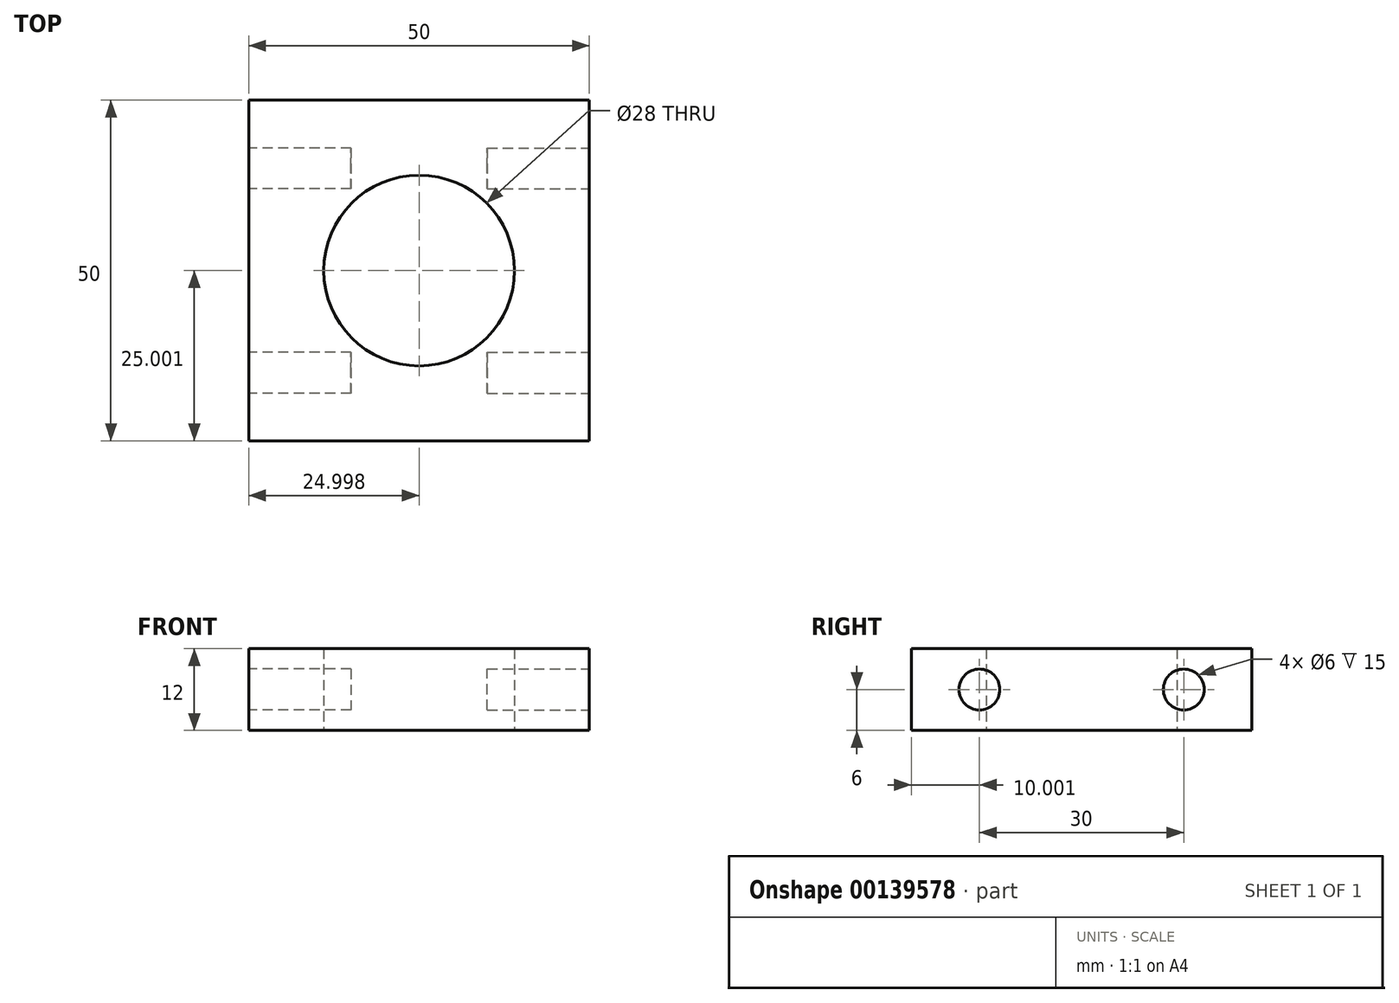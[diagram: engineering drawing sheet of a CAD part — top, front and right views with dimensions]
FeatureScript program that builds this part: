
annotation { "Feature Type Name" : "Feature", "Feature Type Description" : "" }
export const myFeature = defineFeature(function(context is Context, id is Id, definition is map)
    precondition{}
    {
        {
            var Q0;
            Q0=qCreatedBy(makeId("Top.planeOp"),FACE);
            var sketch = newSketch(context, id + "F0", { "sketchPlane" : qUnion([Q0])});
            skLineSegment(sketch, "E0.bottom", {"start": v(-30.5, 20.43) * mm, "end": v(19.5, 20.43) * mm});
            skLineSegment(sketch, "E0.top", {"start": v(-30.5, -29.57) * mm, "end": v(19.5, -29.57) * mm});
            skLineSegment(sketch, "E0.left", {"start": v(-30.5, 20.43) * mm, "end": v(-30.5, -29.57) * mm});
            skLineSegment(sketch, "E0.right", {"start": v(19.5, 20.43) * mm, "end": v(19.5, -29.57) * mm});
            skSolve(sketch);
        }
        {
            var Q0;
            Q0 = qSketchRegion(id + "F0", true);
            extrude(context, id + "F1", {"entities" : qUnion([Q0]), "depth" : 12 * mm});
        }
        {
            var Q0;
            Q0=makeQuery(id+"F1.opExtrude","SWEPT_FACE",FACE,{"disambiguationData":[OSD([sQuery(id+"F0.wireOp",EDGE,"E0.left")])]});
            var sketch = newSketch(context, id + "F2", { "sketchPlane" : qUnion([Q0])});
            skCircle(sketch, "E1", {"center": v(-10.43, 6) * mm, "radius": 3 * mm});
            skCircle(sketch, "E2", {"center": v(19.57, 6) * mm, "radius": 3 * mm});
            skSolve(sketch);
        }
        {
            var Q0;
            Q0=makeQuery(id+"F2.imprint","IMPRINT",FACE,{"disambiguationData":[TD([[makeQuery(id+"F2.imprint","IMPRINT",EDGE,{"derivedFrom":sQuery(id+"F2.wireOp",EDGE,"E1")}),1.0]])]});
            var Q1;
            Q1=makeQuery(id+"F2.imprint","IMPRINT",FACE,{"disambiguationData":[TD([[makeQuery(id+"F2.imprint","IMPRINT",EDGE,{"derivedFrom":sQuery(id+"F2.wireOp",EDGE,"E2")}),1.0]])]});
            extrude(context, id + "F3", {"entities" : qUnion([Q0, Q1]), "operationType" : NewBodyOperationType.REMOVE, "oppositeDirection" : true, "depth" : 15 * mm});
        }
        {
            var Q0;
            Q0=makeQuery(id+"F1.opExtrude","SWEPT_FACE",FACE,{"disambiguationData":[OSD([sQuery(id+"F0.wireOp",EDGE,"E0.right")])]});
            var sketch = newSketch(context, id + "F4", { "sketchPlane" : qUnion([Q0])});
            skCircle(sketch, "E3", {"center": v(10.43, 6) * mm, "radius": 3 * mm});
            skCircle(sketch, "E4", {"center": v(-19.57, 6) * mm, "radius": 3 * mm});
            skSolve(sketch);
        }
        {
            var Q0;
            Q0=makeQuery(id+"F4.imprint","IMPRINT",FACE,{"disambiguationData":[TD([[makeQuery(id+"F4.imprint","IMPRINT",EDGE,{"derivedFrom":sQuery(id+"F4.wireOp",EDGE,"E3")}),1.0]])]});
            var Q1;
            Q1=makeQuery(id+"F4.imprint","IMPRINT",FACE,{"disambiguationData":[TD([[makeQuery(id+"F4.imprint","IMPRINT",EDGE,{"derivedFrom":sQuery(id+"F4.wireOp",EDGE,"E4")}),1.0]])]});
            extrude(context, id + "F5", {"entities" : qUnion([Q0, Q1]), "operationType" : NewBodyOperationType.REMOVE, "oppositeDirection" : true, "depth" : 15 * mm});
        }
        {
            var Q0;
            Q0=makeQuery(id+"F1.opExtrude","CAP_FACE",FACE,{"disambiguationData":[OSD([sQuery(id+"F0.wireOp",EDGE,"E0.bottom"),sQuery(id+"F0.wireOp",EDGE,"E0.top"),sQuery(id+"F0.wireOp",EDGE,"E0.left"),sQuery(id+"F0.wireOp",EDGE,"E0.right")])],"isStart":true});
            var sketch = newSketch(context, id + "F6", { "sketchPlane" : qUnion([Q0])});
            skCircle(sketch, "E5", {"center": v(-5.5, 4.57) * mm, "radius": 14 * mm});
            skSolve(sketch);
        }
        {
            var Q0;
            Q0=makeQuery(id+"F6.imprint","IMPRINT",FACE,{"disambiguationData":[TD([[makeQuery(id+"F6.imprint","IMPRINT",EDGE,{"derivedFrom":sQuery(id+"F6.wireOp",EDGE,"E5")}),1.0]])]});
            extrude(context, id + "F7", {"entities" : qUnion([Q0]), "operationType" : NewBodyOperationType.REMOVE, "endBound" : BoundingType.THROUGH_ALL, "oppositeDirection" : true, "depth" : 25 * mm});
        }
    });
